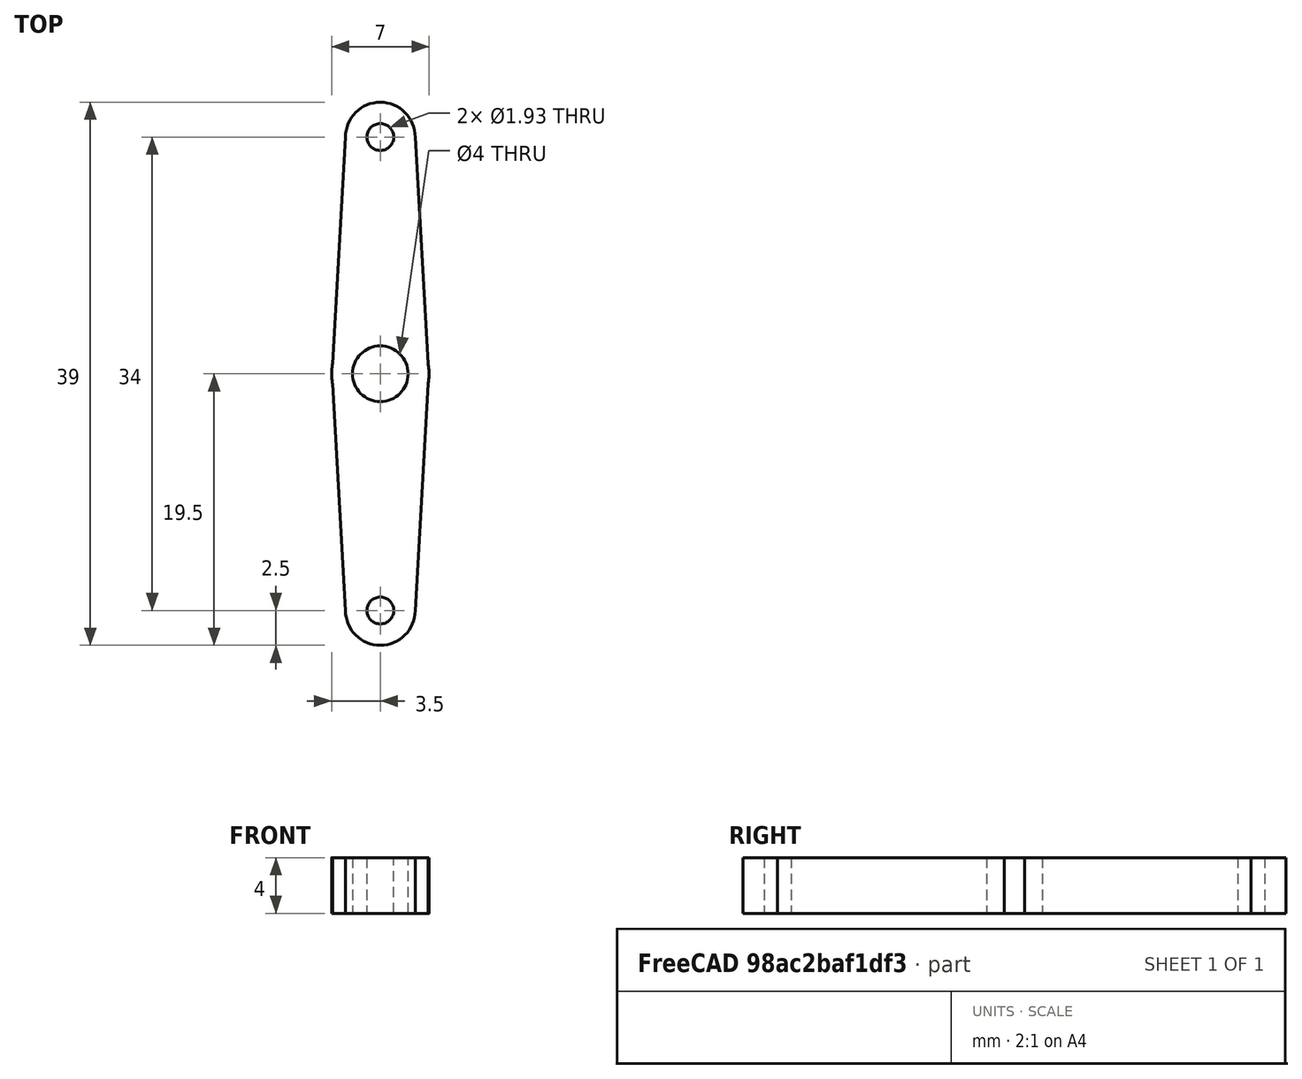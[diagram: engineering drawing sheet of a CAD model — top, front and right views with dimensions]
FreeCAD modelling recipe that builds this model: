
FCSTD DOCUMENT  (FreeCAD 1.0R39319 (Git))
Label: servo_arm
License: All rights reserved
LicenseURL: https://en.wikipedia.org/wiki/All_rights_reserved
objects: Sketcher::SketchObject×1, PartDesign::Pad×1, PartDesign::Body×1
note: 6 computed .brp shape members not serialized (recipe doc carries the construction recipe); baked Part::Feature solids carry a one-line shape summary decoded from their .brp

FEATURE [Sketcher::SketchObject] Sketch001
  ArcFitTolerance = 1e-06
  AttachmentSupport = -> [XY_Plane]
  FullyConstrained = false
  MakeInternals = false
  MapMode = 5
  sketch-geometry (13):
    g0: Circle CenterX=0 CenterY=0 CenterZ=0 NormalX=0 NormalY=0 NormalZ=1 AngleXU=0 Radius=2
    g1: ArcOfCircle CenterX=0 CenterY=0 CenterZ=0 NormalX=0 NormalY=0 NormalZ=1 AngleXU=0 Radius=3.5 StartAngle=2.92858 EndAngle=3.35461
    g2: ArcOfCircle CenterX=0 CenterY=-17 CenterZ=0 NormalX=0 NormalY=0 NormalZ=1 AngleXU=0 Radius=2.5 StartAngle=3.14159 EndAngle=6.28319
    g3: ArcOfCircle CenterX=0 CenterY=17 CenterZ=0 NormalX=0 NormalY=0 NormalZ=1 AngleXU=0 Radius=2.5 StartAngle=0 EndAngle=3.14159
    g4: LineSegment StartX=-2.5 StartY=-17 StartZ=0 EndX=-3.42089 EndY=-0.739919 EndZ=0
    g5: LineSegment StartX=2.5 StartY=-17 StartZ=0 EndX=3.42089 EndY=-0.739919 EndZ=0
    g6: LineSegment StartX=3.42089 StartY=0.739919 StartZ=0 EndX=2.5 EndY=17 EndZ=0
    g7: LineSegment StartX=-3.42089 StartY=0.739919 StartZ=0 EndX=-2.5 EndY=17 EndZ=0
    g8: LineSegment [constr] StartX=2.5 StartY=17 StartZ=0 EndX=-2.5 EndY=17 EndZ=0
    g9: LineSegment [constr] StartX=2.5 StartY=-17 StartZ=0 EndX=-2.5 EndY=-17 EndZ=0
    g10: Circle CenterX=0 CenterY=17 CenterZ=0 NormalX=0 NormalY=0 NormalZ=1 AngleXU=0 Radius=0.965047
    g11: Circle CenterX=0 CenterY=-17 CenterZ=0 NormalX=0 NormalY=0 NormalZ=1 AngleXU=0 Radius=0.965047
    g12: ArcOfCircle CenterX=0 CenterY=0 CenterZ=0 NormalX=0 NormalY=0 NormalZ=1 AngleXU=0 Radius=3.5 StartAngle=6.07017 EndAngle=6.4962
  constraints (31):
    c: Coincident(g0,g-1)
    c: Coincident(g1,g0)
    c: PointOnObject(g3,g-2)
    c: PointOnObject(g2,g-2)
    c: Equal(g3,g2)
    c: Diameter(g3) = 5
    c: Coincident(g8,g6)
    c: Coincident(g8,g7)
    c: PointOnObject(g3,g8)
    c: Horizontal(g8)
    c: Vertical(g7,g4)
    c: Horizontal(g7,g6)
    c: Horizontal(g5,g4)
    c: Diameter(g0) = 4
    c: Diameter(g1) = 7
    c: DistanceY(g0,g3) = 17
    c: Coincident(g9,g5)
    c: Coincident(g9,g4)
    c: Horizontal(g9)
    c: PointOnObject(g2,g9)
    c: Equal(g11,g10)
    c: Coincident(g3,g6)
    c: Coincident(g3,g7)
    c: Coincident(g1,g7)
    c: Coincident(g12,g6)
    c: Equal(g1,g12)
    c: Coincident(g1,g4)
    c: Coincident(g1,g12)
    c: Coincident(g12,g5)
    c: Coincident(g2,g5)
    c: Coincident(g2,g4)
FEATURE [PartDesign::Pad] Pad
  Direction = (0,0,1)
  Length = 4
  Length2 = 10
  Profile = -> Sketch001
  ReferenceAxis = -> Sketch001 [N_Axis]
  Refine = true
  Suppressed = false
  Type = 0
FEATURE [PartDesign::Body] Body
  AllowCompound = false
  Group = -> [Sketch001,Pad]
  Origin = -> Origin
  Tip = -> Pad
